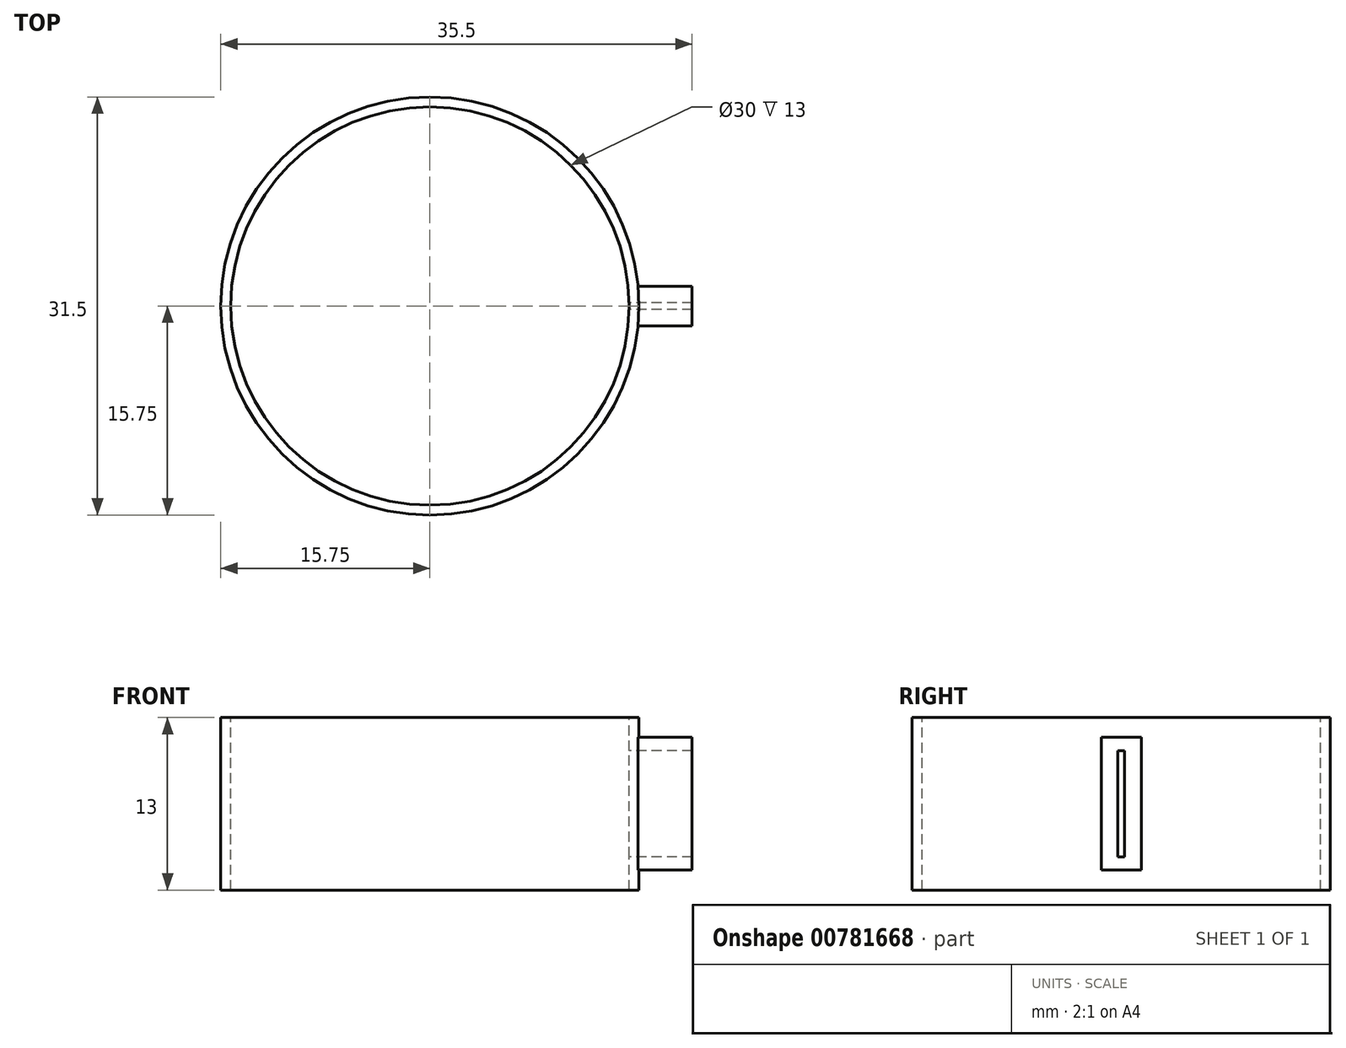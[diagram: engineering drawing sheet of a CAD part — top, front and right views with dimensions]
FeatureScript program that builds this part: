
annotation { "Feature Type Name" : "Feature", "Feature Type Description" : "" }
export const myFeature = defineFeature(function(context is Context, id is Id, definition is map)
    precondition{}
    {
        {
            var Q0;
            Q0=qCreatedBy(makeId("Top.planeOp"),FACE);
            var sketch = newSketch(context, id + "F0", { "sketchPlane" : qUnion([Q0])});
            skCircle(sketch, "E0", {"center": v(0, 0) * mm, "radius": 15.75 * mm});
            skSolve(sketch);
        }
        {
            var Q0;
            Q0=qSketchRegion(id+"F0",true);
            extrude(context, id + "F1", {"entities" : qUnion([Q0]), "depth" : 13 * mm, "offsetDistance" : 25 * mm});
        }
        {
            var Q0;
            Q0=qCreatedBy(makeId("Right.planeOp"),FACE);
            var sketch = newSketch(context, id + "F2", { "sketchPlane" : qUnion([Q0])});
            skLineSegment(sketch, "E1.bottom", {"start": v(-0.25, 10.5) * mm, "end": v(0.25, 10.5) * mm});
            skLineSegment(sketch, "E1.top", {"start": v(-0.25, 2.5) * mm, "end": v(0.25, 2.5) * mm});
            skLineSegment(sketch, "E1.left", {"start": v(-0.25, 10.5) * mm, "end": v(-0.25, 2.5) * mm});
            skLineSegment(sketch, "E1.right", {"start": v(0.25, 10.5) * mm, "end": v(0.25, 2.5) * mm});
            skLineSegment(sketch, "E2", {"start": v(0, 0) * mm, "end": v(0, 2.5) * mm, "construction": true});
            skLineSegment(sketch, "E3.0", {"start": v(-15.75, 13) * mm, "end": v(15.75, 13) * mm});
            skLineSegment(sketch, "E4", {"start": v(0, 10.5) * mm, "end": v(0, 13) * mm, "construction": true});
            skLineSegment(sketch, "E5.bottom", {"start": v(-1.5, 11.5) * mm, "end": v(1.5, 11.5) * mm});
            skLineSegment(sketch, "E5.top", {"start": v(-1.5, 1.5) * mm, "end": v(1.5, 1.5) * mm});
            skLineSegment(sketch, "E5.left", {"start": v(-1.5, 11.5) * mm, "end": v(-1.5, 1.5) * mm});
            skLineSegment(sketch, "E5.right", {"start": v(1.5, 11.5) * mm, "end": v(1.5, 1.5) * mm});
            skLineSegment(sketch, "E6", {"start": v(0, 0) * mm, "end": v(0, 1.5) * mm, "construction": true});
            skLineSegment(sketch, "E7", {"start": v(0, 13) * mm, "end": v(0, 11.5) * mm, "construction": true});
            skLineSegment(sketch, "E8", {"start": v(0.25, 10.5) * mm, "end": v(0.25, 11.5) * mm, "construction": true});
            skLineSegment(sketch, "E9", {"start": v(0.25, 2.5) * mm, "end": v(0.25, 1.5) * mm, "construction": true});
            skSolve(sketch);
        }
        {
            var Q0;
            Q0=qSketchRegion(id+"F2",true);
            extrude(context, id + "F3", {"entities" : qUnion([Q0]), "operationType" : NewBodyOperationType.ADD, "depth" : 19.75 * mm, "offsetDistance" : 25 * mm});
        }
        {
            var Q0;
            Q0=qCreatedBy(makeId("Front.planeOp"),FACE);
            var sketch = newSketch(context, id + "F4", { "sketchPlane" : qUnion([Q0])});
            skLineSegment(sketch, "E10", {"start": v(0, 0) * mm, "end": v(0, 21.4) * mm, "construction": true});
            skSolve(sketch);
        }
        {
            var Q0;
            Q0=makeQuery(id+"F1.opExtrude","CAP_FACE",FACE,{"disambiguationData":[OSD([sQuery(id+"F0.wireOp",EDGE,"E0")])],"isStart":false});
            var sketch = newSketch(context, id + "F5", { "sketchPlane" : qUnion([Q0])});
            skCircle(sketch, "E11", {"center": v(0, 0) * mm, "radius": 15 * mm});
            skSolve(sketch);
        }
        {
            var Q0;
            Q0=qSketchRegion(id+"F5",true);
            extrude(context, id + "F6", {"entities" : qUnion([Q0]), "operationType" : NewBodyOperationType.REMOVE, "oppositeDirection" : true, "depth" : 25 * mm, "offsetDistance" : 25 * mm});
        }
        {
            var Q0;
            Q0=qCreatedBy(makeId("Right.planeOp"),FACE);
            var sketch = newSketch(context, id + "F7", { "sketchPlane" : qUnion([Q0])});
            skLineSegment(sketch, "E12.0", {"start": v(-0.25, 10.5) * mm, "end": v(-0.25, 2.5) * mm});
            skLineSegment(sketch, "E12.1", {"start": v(0.25, 10.5) * mm, "end": v(0.25, 2.5) * mm});
            skLineSegment(sketch, "E12.2", {"start": v(-0.25, 10.5) * mm, "end": v(0.25, 10.5) * mm});
            skLineSegment(sketch, "E12.3", {"start": v(-0.25, 2.5) * mm, "end": v(0.25, 2.5) * mm});
            skSolve(sketch);
        }
        {
            var Q0;
            Q0=qSketchRegion(id+"F7",true);
            extrude(context, id + "F8", {"entities" : qUnion([Q0]), "operationType" : NewBodyOperationType.REMOVE, "depth" : 25 * mm, "offsetDistance" : 25 * mm});
        }
    });
